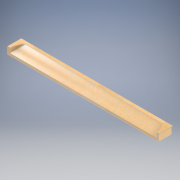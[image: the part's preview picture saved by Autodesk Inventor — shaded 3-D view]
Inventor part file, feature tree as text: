
AUTODESK INVENTOR PART (.ipt)
format: ipt  version: 2022.2 (Build 262287010, 287A)  size: 201,728 bytes
history: native  units: in
note: dims shown in document units (in); Inventor stores cm internally (conversion verified against a paired STEP export)
features: revolve x2, direct_edit x1, extrude x1, sketch x1, projected_geometry x1
ambient origin geometry x8: Origin, YZ Plane, XZ Plane, XY Plane, X Axis, Y Axis, Z Axis, Center Point
bodies: Solid1 (feature_tree), Body1 (feature_tree)
feature tree (6):
  direct_edit  "Direct Edit1"
  extrude  "Extrusion1"  TaperAngle=180.0deg  [1 undecoded]
  sketch  "Sketch1"  dims[d0=-0.6184in d1=180.0deg d2=0.375in d3=0.0in]
  projected_geometry  "Projected Loop1"
  revolve  "Rotate1"  [1 undecoded]
  revolve  "Rotate2"  [1 undecoded]
note: 3 required parameter values undecoded (feature->parameter linkage not recoverable at this tier; creation-order binding heuristic only, values carry confidence <= 0.55)